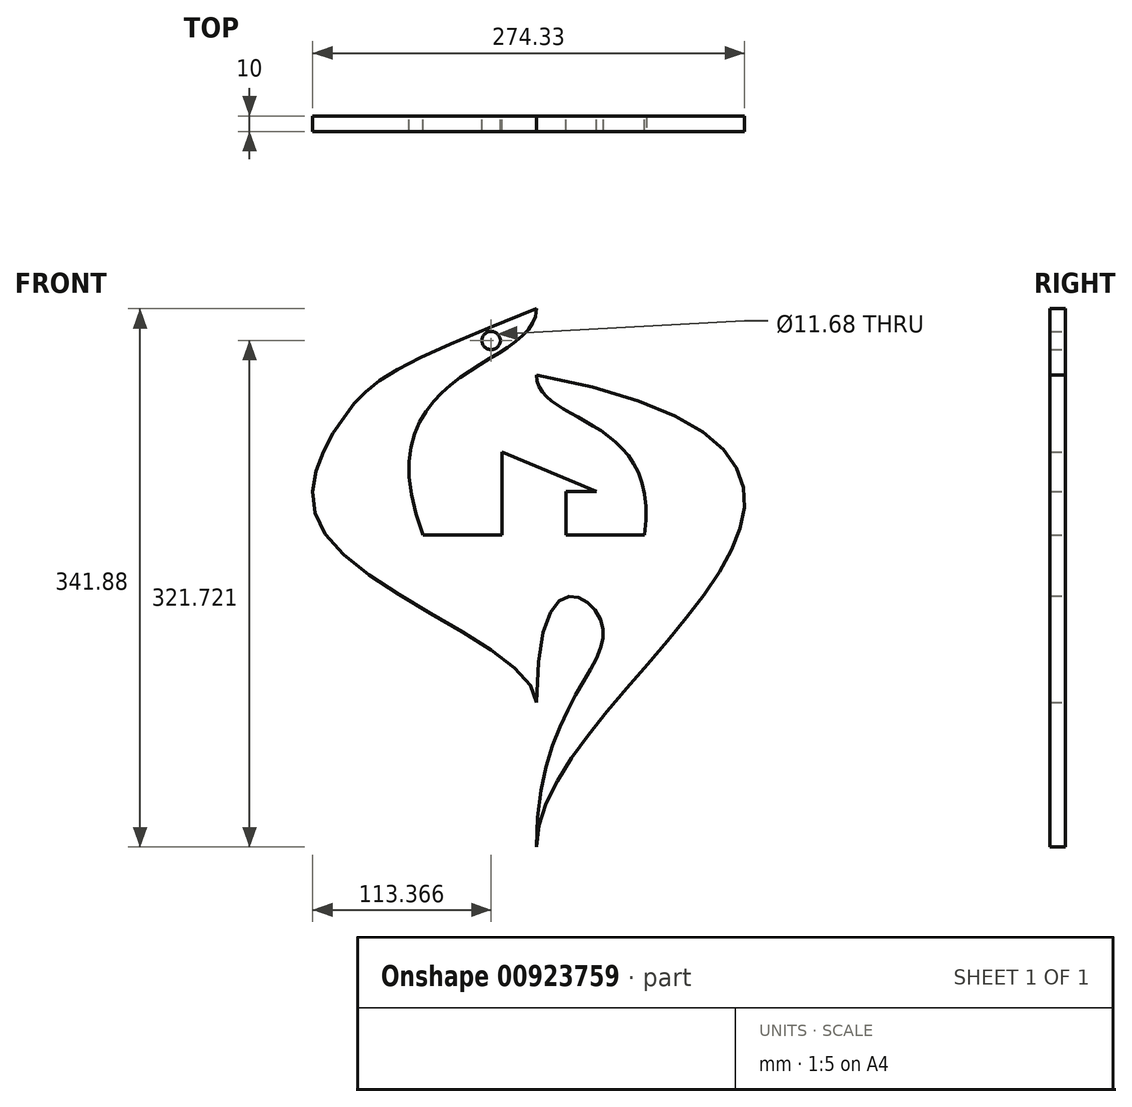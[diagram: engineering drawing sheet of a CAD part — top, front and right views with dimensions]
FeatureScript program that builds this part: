
annotation { "Feature Type Name" : "Feature", "Feature Type Description" : "" }
export const myFeature = defineFeature(function(context is Context, id is Id, definition is map)
    precondition{}
    {
        {
            var Q0;
            Q0=qCreatedBy(makeId("Front.planeOp"),FACE);
            var sketch = newSketch(context, id + "F0", { "sketchPlane" : qUnion([Q0])});
            skLineSegment(sketch, "E0", {"start": v(18.73, 36.47) * mm, "end": v(68.73, 36.47) * mm});
            skLineSegment(sketch, "E1", {"start": v(-21.92, 36.47) * mm, "end": v(-71.92, 36.47) * mm});
            skLineSegment(sketch, "E2", {"start": v(18.73, 36.47) * mm, "end": v(18.73, 64.05) * mm});
            skLineSegment(sketch, "E3", {"start": v(18.73, 64.05) * mm, "end": v(38.2, 64.05) * mm});
            skLineSegment(sketch, "E4", {"start": v(38.2, 64.05) * mm, "end": v(-21.92, 89.12) * mm});
            skLineSegment(sketch, "E5", {"start": v(-21.92, 89.12) * mm, "end": v(-21.92, 36.47) * mm});
            skPoint(sketch, "E6.startSnap0", {"position": v(8.14, 76.58) * mm});
            skFitSpline(sketch, "E7", {"points": [v(68.73, 36.47) * mm, v(0, 138.17) * mm], "startDerivative": vector(32.47, 230.95) * mm, "endDerivative": vector(0, 95.52) * mm});
            skFitSpline(sketch, "E8", {"points": [v(0, 138.17) * mm, v(0, -161.73) * mm], "startDerivative": vector(892.17, -168.93) * mm, "endDerivative": vector(0, -309.04) * mm});
            skFitSpline(sketch, "E9", {"points": [v(-71.92, 36.47) * mm, v(0, 180.16) * mm], "startDerivative": vector(-123.98, 321.34) * mm, "endDerivative": vector(0, 115.09) * mm});
            skFitSpline(sketch, "E10", {"points": [v(0, 180.16) * mm, v(-123.42, 109.68) * mm, v(-133.8, 36.38) * mm, v(0, -69.95) * mm], "startDerivative": vector(-775.89, -310.2) * mm, "endDerivative": vector(0, -248.93) * mm});
            skFitSpline(sketch, "E11", {"points": [v(0, -69.95) * mm, v(41.16, -18.25) * mm, v(0, -161.73) * mm], "startDerivative": vector(0, 678.5) * mm, "endDerivative": vector(0, -458.5) * mm});
            skCircle(sketch, "E12", {"center": v(-28.8, 160) * mm, "radius": 5.84 * mm});
            skCircle(sketch, "E13", {"center": v(-28.8, 160) * mm, "radius": 5.07 * mm});
            skSolve(sketch);
        }
        {
            var Q0;
            Q0=makeQuery(id+"F0.imprint","IMPRINT",FACE,{"disambiguationData":[TD([[makeQuery(id+"F0.imprint","IMPRINT",EDGE,{"derivedFrom":sQuery(id+"F0.wireOp",EDGE,"E0")}),-1.0]])]});
            extrude(context, id + "F1", {"entities" : qUnion([Q0]), "depth" : 10 * mm, "offsetDistance" : 25 * mm});
        }
    });
